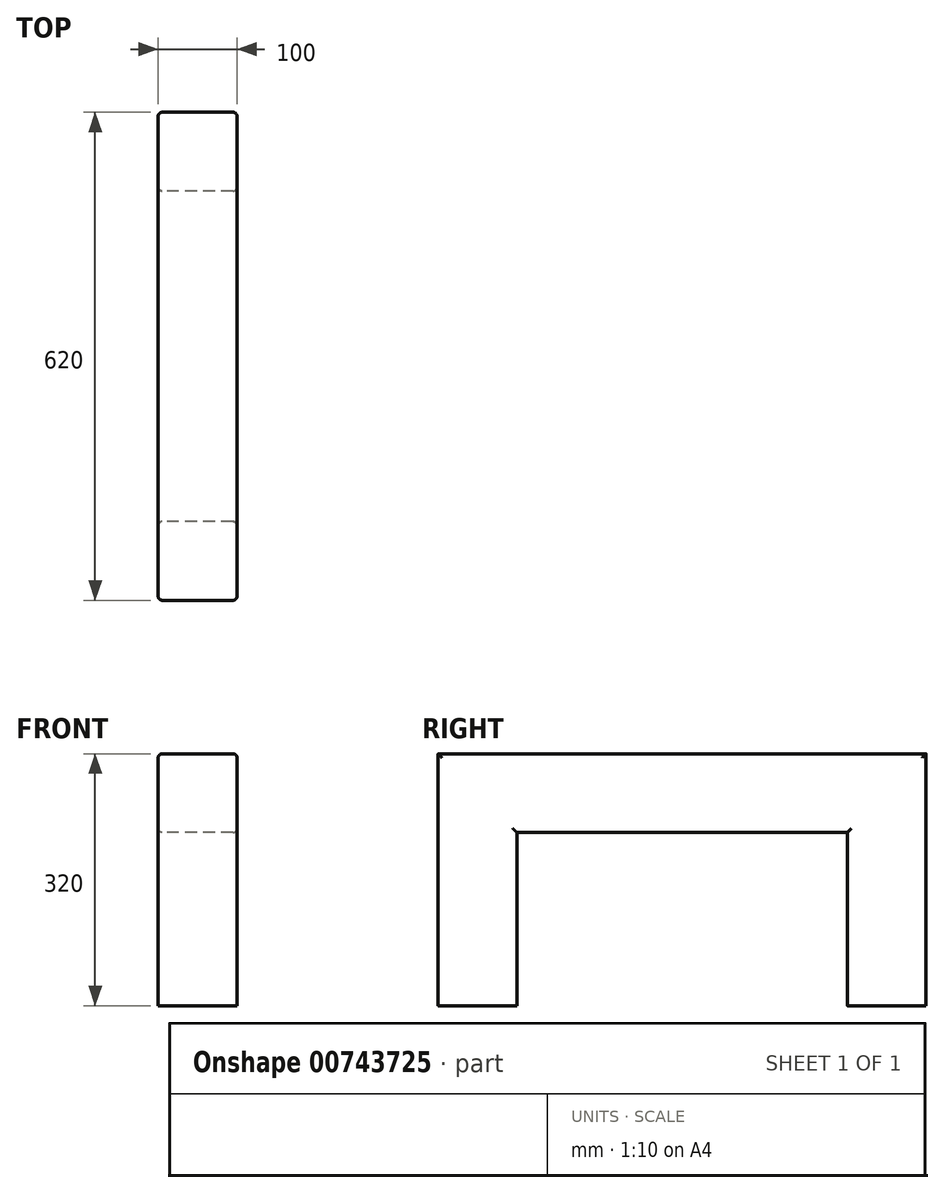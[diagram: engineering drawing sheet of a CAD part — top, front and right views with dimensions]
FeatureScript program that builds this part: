
annotation { "Feature Type Name" : "Feature", "Feature Type Description" : "" }
export const myFeature = defineFeature(function(context is Context, id is Id, definition is map)
    precondition{}
    {
        {
            var Q0;
            Q0=qCreatedBy(makeId("Right.planeOp"),FACE);
            var sketch = newSketch(context, id + "F0", { "sketchPlane" : qUnion([Q0])});
            skLineSegment(sketch, "E0", {"start": v(0, 0) * mm, "end": v(0, 220) * mm});
            skLineSegment(sketch, "E1", {"start": v(0, 220) * mm, "end": v(-420, 220) * mm});
            skLineSegment(sketch, "E2", {"start": v(-420, 220) * mm, "end": v(-420, 0) * mm});
            skLineSegment(sketch, "E3", {"start": v(-420, 0) * mm, "end": v(-520, 0) * mm});
            skLineSegment(sketch, "E4", {"start": v(-520, 0) * mm, "end": v(-520, 320) * mm});
            skLineSegment(sketch, "E5", {"start": v(-520, 320) * mm, "end": v(100, 320) * mm});
            skLineSegment(sketch, "E6", {"start": v(100, 320) * mm, "end": v(100, 0) * mm});
            skLineSegment(sketch, "E7", {"start": v(100, 0) * mm, "end": v(0, 0) * mm});
            skSolve(sketch);
        }
        {
            var Q0;
            Q0 = qSketchRegion(id + "F0", true);
            extrude(context, id + "F1", {"entities" : qUnion([Q0]), "depth" : 100 * mm, "offsetDistance" : 25 * mm});
        }
        {
            var Q0;
            Q0=makeQuery(id+"F1.opExtrude","CAP_EDGE",EDGE,{"disambiguationData":[OSD([sQuery(id+"F0.wireOp",EDGE,"E4")])],"isStart":false});
            var Q1;
            Q1=makeQuery(id+"F1.opExtrude","CAP_EDGE",EDGE,{"disambiguationData":[OSD([sQuery(id+"F0.wireOp",EDGE,"E2")])],"isStart":false});
            var Q2;
            Q2=makeQuery(id+"F1.opExtrude","CAP_EDGE",EDGE,{"disambiguationData":[OSD([sQuery(id+"F0.wireOp",EDGE,"E1")])],"isStart":false});
            var Q3;
            Q3=makeQuery(id+"F1.opExtrude","CAP_EDGE",EDGE,{"disambiguationData":[OSD([sQuery(id+"F0.wireOp",EDGE,"E0")])],"isStart":false});
            var Q4;
            Q4=makeQuery(id+"F1.opExtrude","CAP_EDGE",EDGE,{"disambiguationData":[OSD([sQuery(id+"F0.wireOp",EDGE,"E6")])],"isStart":false});
            var Q5;
            Q5=makeQuery(id+"F1.opExtrude","CAP_EDGE",EDGE,{"disambiguationData":[OSD([sQuery(id+"F0.wireOp",EDGE,"E4")])],"isStart":true});
            var Q6;
            Q6=makeQuery(id+"F1.opExtrude","CAP_EDGE",EDGE,{"disambiguationData":[OSD([sQuery(id+"F0.wireOp",EDGE,"E0")])],"isStart":true});
            var Q7;
            Q7=makeQuery(id+"F1.opExtrude","CAP_EDGE",EDGE,{"disambiguationData":[OSD([sQuery(id+"F0.wireOp",EDGE,"E1")])],"isStart":true});
            var Q8;
            Q8=makeQuery(id+"F1.opExtrude","CAP_EDGE",EDGE,{"disambiguationData":[OSD([sQuery(id+"F0.wireOp",EDGE,"E2")])],"isStart":true});
            var Q9;
            Q9=makeQuery(id+"F1.opExtrude","CAP_EDGE",EDGE,{"disambiguationData":[OSD([sQuery(id+"F0.wireOp",EDGE,"E6")])],"isStart":true});
            var Q10;
            Q10=makeQuery(id+"F1.opExtrude","CAP_EDGE",EDGE,{"disambiguationData":[OSD([sQuery(id+"F0.wireOp",EDGE,"E5")])],"isStart":true});
            var Q11;
            Q11=makeQuery(id+"F1.opExtrude","CAP_EDGE",EDGE,{"disambiguationData":[OSD([sQuery(id+"F0.wireOp",EDGE,"E5")])],"isStart":false});
            fillet(context, id + "F2", {"entities" : qUnion([Q0, Q1, Q2, Q3, Q4, Q5, Q6, Q7, Q8, Q9, Q10, Q11]), "radius" : 5 * mm, "tangentPropagation" : true, "allowEdgeOverflow" : false});
        }
    });
